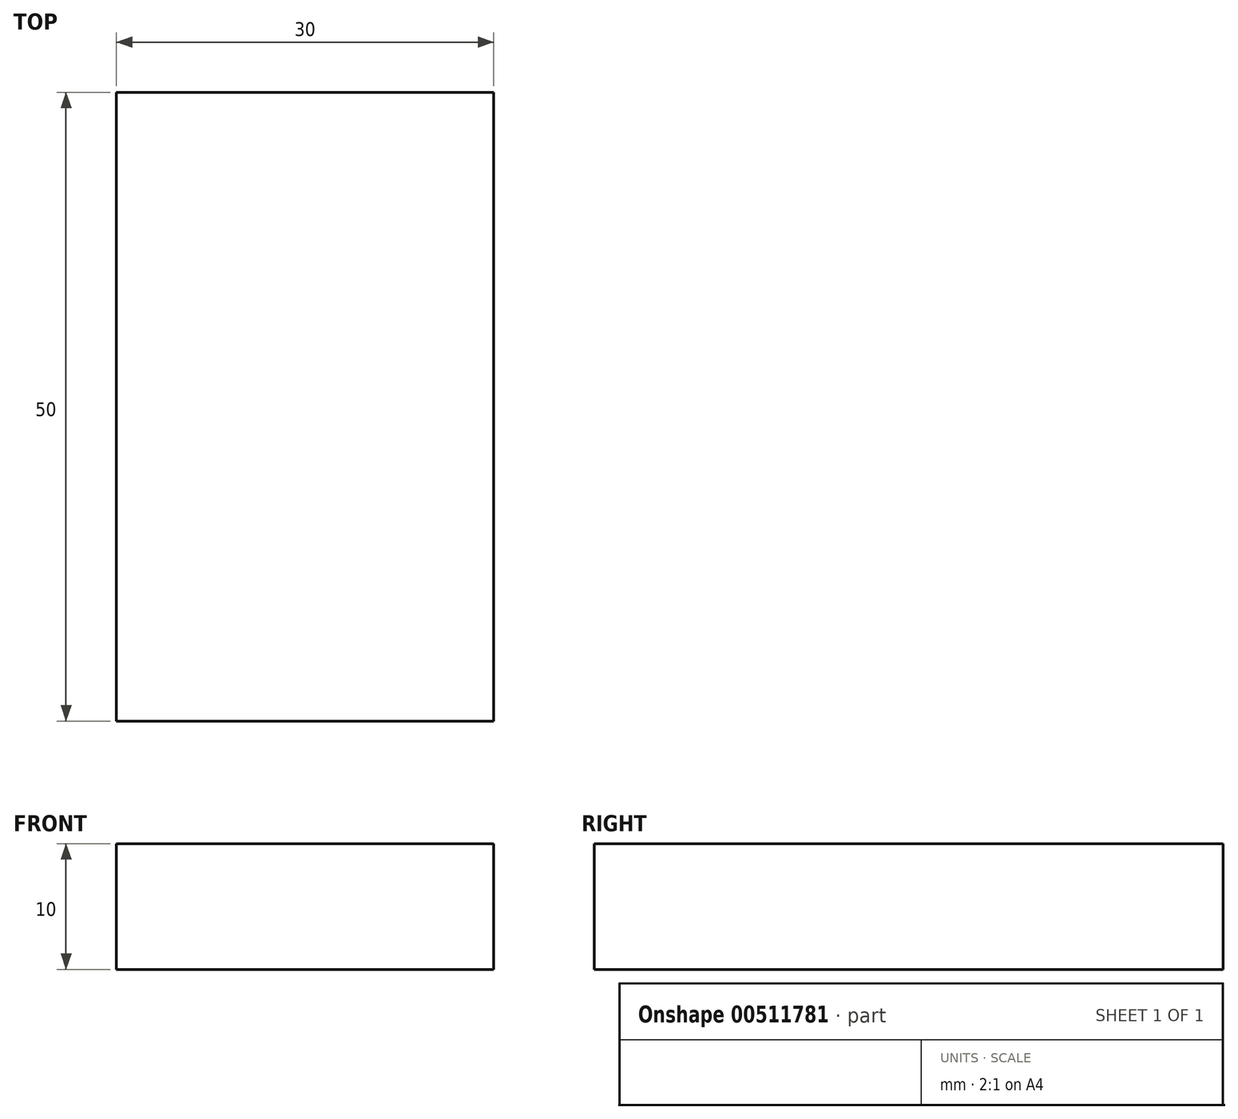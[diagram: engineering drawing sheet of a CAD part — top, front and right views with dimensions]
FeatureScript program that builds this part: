
annotation { "Feature Type Name" : "Feature", "Feature Type Description" : "" }
export const myFeature = defineFeature(function(context is Context, id is Id, definition is map)
    precondition{}
    {
        {
            var Q0;
            Q0=qCreatedBy(makeId("Top.planeOp"),FACE);
            var sketch = newSketch(context, id + "F0", { "sketchPlane" : qUnion([Q0])});
            skLineSegment(sketch, "E0.bottom", {"start": v(15, -25) * mm, "end": v(-15, -25) * mm});
            skLineSegment(sketch, "E0.top", {"start": v(15, 25) * mm, "end": v(-15, 25) * mm});
            skLineSegment(sketch, "E0.left", {"start": v(15, -25) * mm, "end": v(15, 25) * mm});
            skLineSegment(sketch, "E0.right", {"start": v(-15, -25) * mm, "end": v(-15, 25) * mm});
            skPoint(sketch, "E0.middle", {"position": v(0, 0) * mm});
            skSolve(sketch);
        }
        {
            var Q0;
            Q0 = qSketchRegion(id + "F0", true);
            extrude(context, id + "F1", {"entities" : qUnion([Q0]), "depth" : 10 * mm});
        }
    });
